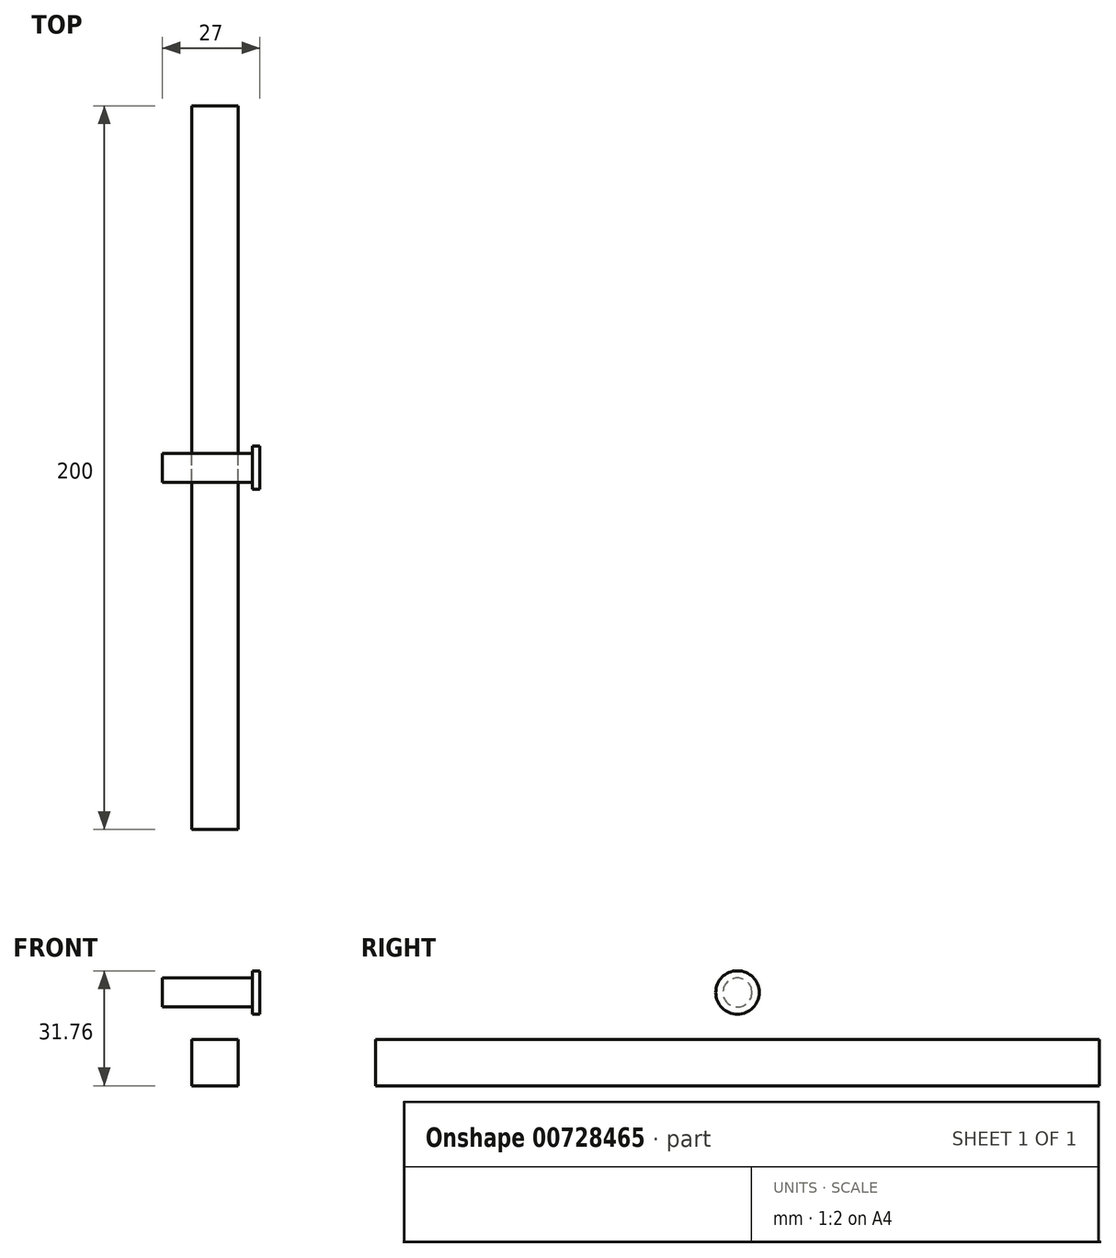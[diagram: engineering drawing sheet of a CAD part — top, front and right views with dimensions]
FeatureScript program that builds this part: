
annotation { "Feature Type Name" : "Feature", "Feature Type Description" : "" }
export const myFeature = defineFeature(function(context is Context, id is Id, definition is map)
    precondition{}
    {
        {
            var Q0;
            Q0=qCreatedBy(makeId("Right.planeOp"),FACE);
            var sketch = newSketch(context, id + "F0", { "sketchPlane" : qUnion([Q0])});
            skCircle(sketch, "E0", {"center": v(0, 0) * mm, "radius": 6 * mm});
            skSolve(sketch);
        }
        {
            var Q0;
            Q0 = qSketchRegion(id + "F0", true);
            extrude(context, id + "F1", {"entities" : qUnion([Q0]), "depth" : 2 * mm, "offsetDistance" : 25 * mm});
        }
        {
            var Q0;
            Q0=qCreatedBy(makeId("Right.planeOp"),FACE);
            var sketch = newSketch(context, id + "F2", { "sketchPlane" : qUnion([Q0])});
            skCircle(sketch, "E1", {"center": v(0, 0) * mm, "radius": 4 * mm});
            skSolve(sketch);
        }
        {
            var Q0;
            Q0=makeQuery(id+"F2.imprint","IMPRINT",FACE,{"disambiguationData":[TD([[makeQuery(id+"F2.imprint","IMPRINT",EDGE,{"derivedFrom":sQuery(id+"F2.wireOp",EDGE,"E1")}),1.0]])]});
            extrude(context, id + "F3", {"entities" : qUnion([Q0]), "operationType" : NewBodyOperationType.ADD, "oppositeDirection" : true, "depth" : 25 * mm, "offsetDistance" : 25 * mm});
        }
        {
            var Q0;
            Q0=qCreatedBy(makeId("Right.planeOp"),FACE);
            cPlane(context, id + "F4", {"entities" : qUnion([Q0]), "cplaneType" : CPlaneType.OFFSET, "offset" : 2 * mm, "width" : 150 * mm, "height" : 150 * mm});
        }
        {
            var Q0;
            Q0=qCreatedBy(id+"F4.planeOp",FACE);
            var sketch = newSketch(context, id + "F5", { "sketchPlane" : qUnion([Q0])});
            skCircle(sketch, "E2", {"center": v(0, 0) * mm, "radius": 2 * mm});
            skSolve(sketch);
        }
        {
            var Q0;
            Q0=sQuery(id+"F5.wireOp",EDGE,"E2");
            extrude(context, id + "F6", {"bodyType" : ToolBodyType.SURFACE, "surfaceEntities" : qUnion([Q0]), "oppositeDirection" : true, "depth" : 27 * mm, "offsetDistance" : 25 * mm});
        }
        {
            var Q0;
            Q0=qCreatedBy(makeId("Right.planeOp"),FACE);
            cPlane(context, id + "F7", {"entities" : qUnion([Q0]), "cplaneType" : CPlaneType.OFFSET, "offset" : 4 * mm, "oppositeDirection" : true, "width" : 150 * mm, "height" : 150 * mm});
        }
        {
            var Q0;
            Q0=qCreatedBy(id+"F7.planeOp",FACE);
            cPlane(context, id + "F8", {"entities" : qUnion([Q0]), "cplaneType" : CPlaneType.OFFSET, "offset" : 12.8 * mm, "oppositeDirection" : true, "width" : 150 * mm, "height" : 150 * mm});
        }
        {
            var Q0;
            Q0=qCreatedBy(makeId("Front.planeOp"),FACE);
            var sketch = newSketch(context, id + "F9", { "sketchPlane" : qUnion([Q0])});
            skLineSegment(sketch, "E3.bottom", {"start": v(-16.8, -12.96) * mm, "end": v(-4, -12.96) * mm});
            skLineSegment(sketch, "E3.top", {"start": v(-16.8, -25.76) * mm, "end": v(-4, -25.76) * mm});
            skLineSegment(sketch, "E3.left", {"start": v(-16.8, -12.96) * mm, "end": v(-16.8, -25.76) * mm});
            skLineSegment(sketch, "E3.right", {"start": v(-4, -12.96) * mm, "end": v(-4, -25.76) * mm});
            skSolve(sketch);
        }
        {
            var Q0;
            Q0=makeQuery(id+"F9.imprint","IMPRINT",FACE,{"disambiguationData":[TD([[makeQuery(id+"F9.imprint","IMPRINT",EDGE,{"derivedFrom":sQuery(id+"F9.wireOp",EDGE,"E3.bottom")}),-1.0]])]});
            extrude(context, id + "F10", {"entities" : qUnion([Q0]), "depth" : 100 * mm, "offsetDistance" : 25 * mm});
        }
        {
            var Q0;
            Q0=makeQuery(id+"F10.opExtrude","CAP_FACE",FACE,{"disambiguationData":[OSD([sQuery(id+"F9.wireOp",EDGE,"E3.bottom"),sQuery(id+"F9.wireOp",EDGE,"E3.top"),sQuery(id+"F9.wireOp",EDGE,"E3.left"),sQuery(id+"F9.wireOp",EDGE,"E3.right")])],"isStart":false});
            extrude(context, id + "F11", {"entities" : qUnion([Q0]), "operationType" : NewBodyOperationType.ADD, "oppositeDirection" : true, "depth" : 200 * mm, "offsetDistance" : 25 * mm});
        }
        {
            var Q0;
            Q0=qCreatedBy(id+"F7.planeOp",FACE);
            var sketch = newSketch(context, id + "F12", { "sketchPlane" : qUnion([Q0])});
            skLineSegment(sketch, "E4.bottom", {"start": v(-30.39, 0) * mm, "end": v(30.39, 0) * mm});
            skLineSegment(sketch, "E4.top", {"start": v(-30.39, -25.44) * mm, "end": v(30.39, -25.44) * mm});
            skLineSegment(sketch, "E4.left", {"start": v(-30.39, 0) * mm, "end": v(-30.39, -25.44) * mm});
            skLineSegment(sketch, "E4.right", {"start": v(30.39, 0) * mm, "end": v(30.39, -25.44) * mm});
            skSolve(sketch);
        }
        {
            var Q0;
            Q0=qCreatedBy(id+"F7.planeOp",FACE);
            var sketch = newSketch(context, id + "F13", { "sketchPlane" : qUnion([Q0])});
            skLineSegment(sketch, "E5", {"start": v(-30.16, 0) * mm, "end": v(-7.59, 13.3) * mm});
            skLineSegment(sketch, "E6", {"start": v(7.6, 13.33) * mm, "end": v(30.39, 0) * mm});
            skPoint(sketch, "E7.visualSharp", {"position": v(0, 17.78) * mm});
            skArc(sketch, "E7.filletArc", {"start": v(7.6, 13.33) * mm, "mid": v(0, 15.38) * mm, "end": v(-7.59, 13.3) * mm});
            skSolve(sketch);
        }
        {
            var Q0;
            Q0=sQuery(id+"F13.wireOp",EDGE,"E5");
            var Q1;
            Q1=sQuery(id+"F13.wireOp",EDGE,"E7.filletArc");
            var Q2;
            Q2=sQuery(id+"F13.wireOp",EDGE,"E6");
            var Q3;
            Q3=sQuery(id+"F12.wireOp",EDGE,"E4.right");
            var Q4;
            Q4=sQuery(id+"F12.wireOp",EDGE,"E4.top");
            var Q5;
            Q5=sQuery(id+"F12.wireOp",EDGE,"E4.left");
            extrude(context, id + "F14", {"bodyType" : ToolBodyType.SURFACE, "surfaceEntities" : qUnion([Q0, Q1, Q2, Q3, Q4, Q5]), "depth" : 1 * mm, "offsetDistance" : 25 * mm});
        }
    });
